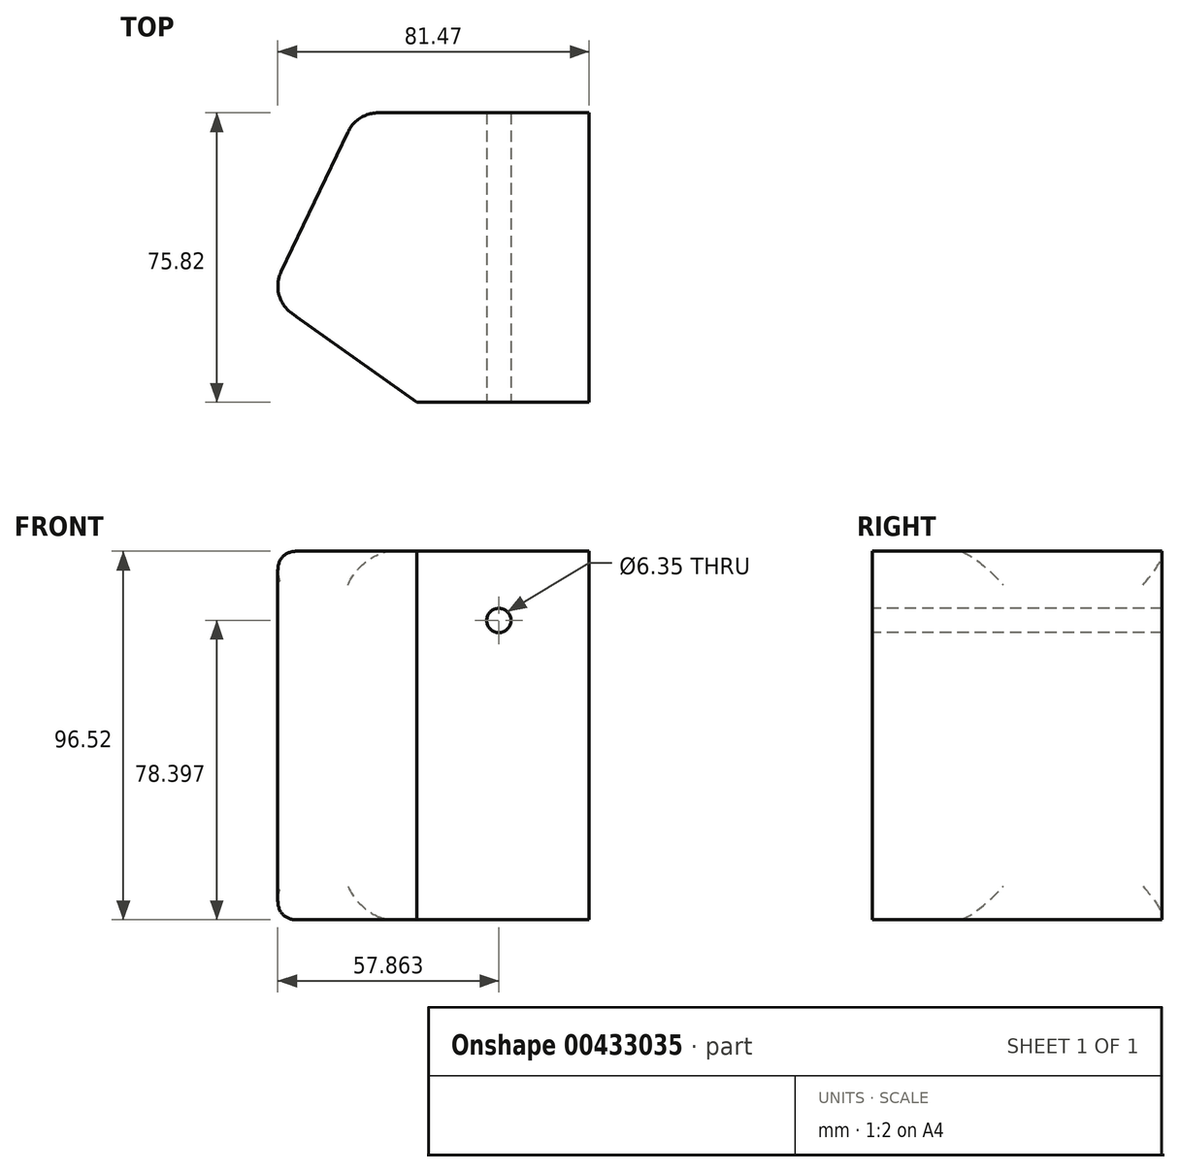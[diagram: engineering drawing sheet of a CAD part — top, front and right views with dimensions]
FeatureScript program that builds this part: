
annotation { "Feature Type Name" : "Feature", "Feature Type Description" : "" }
export const myFeature = defineFeature(function(context is Context, id is Id, definition is map)
    precondition{}
    {
        {
            var Q0;
            Q0=qCreatedBy(makeId("Top.planeOp"),FACE);
            var sketch = newSketch(context, id + "F0", { "sketchPlane" : qUnion([Q0])});
            skLineSegment(sketch, "E0", {"start": v(15.67, -27.58) * mm, "end": v(60.7, -27.58) * mm});
            skLineSegment(sketch, "E1", {"start": v(60.7, -27.58) * mm, "end": v(60.7, 48.24) * mm});
            skLineSegment(sketch, "E2", {"start": v(60.7, 48.24) * mm, "end": v(0, 48.24) * mm});
            skLineSegment(sketch, "E3", {"start": v(0, 48.24) * mm, "end": v(-23.09, 0) * mm});
            skLineSegment(sketch, "E4", {"start": v(-23.09, 0) * mm, "end": v(15.67, -27.58) * mm});
            skSolve(sketch);
        }
        {
            var Q0;
            Q0=makeQuery(id+"F0.imprint","IMPRINT",FACE,{"disambiguationData":[TD([[makeQuery(id+"F0.imprint","IMPRINT",EDGE,{"derivedFrom":sQuery(id+"F0.wireOp",EDGE,"E0")}),1.0]])]});
            extrude(context, id + "F1", {"entities" : qUnion([Q0]), "depth" : 96.52 * mm});
        }
        {
            var Q0;
            Q0=makeQuery(id+"F1.opExtrude","SWEPT_FACE",FACE,{"disambiguationData":[OSD([sQuery(id+"F0.wireOp",EDGE,"E3")])]});
            fillet(context, id + "F2", {"entities" : qUnion([Q0]), "radius" : 8.78 * mm, "tangentPropagation" : true, "allowEdgeOverflow" : false});
        }
        {
            var Q0;
            Q0=makeQuery(id+"F1.opExtrude","SWEPT_FACE",FACE,{"disambiguationData":[OSD([sQuery(id+"F0.wireOp",EDGE,"E0")])]});
            var sketch = newSketch(context, id + "F3", { "sketchPlane" : qUnion([Q0])});
            skCircle(sketch, "E5", {"center": v(37.1, 78.4) * mm, "radius": 11.72 * mm});
            skSolve(sketch);
        }
        {
            var Q0;
            Q0=sQuery(id+"F3.wireOp",VERTEX,"E5.center");
            var Q1;
            Q1=makeQuery(id+"F1.opExtrude","SWEPT_BODY",BODY,{"disambiguationData":[OSD([sQuery(id+"F0.wireOp",EDGE,"E0"),sQuery(id+"F0.wireOp",EDGE,"E1"),sQuery(id+"F0.wireOp",EDGE,"E2"),sQuery(id+"F0.wireOp",EDGE,"E3"),sQuery(id+"F0.wireOp",EDGE,"E4")])]});
            hole(context, id + "F4", {"style" : HoleStyle.SIMPLE, "endStyle" : HoleEndStyle.THROUGH, "holeDiameter" : 6.35 * mm, "isTappedThrough" : true, "tappedDepth" : 12.7 * mm, "tapClearance" : 3, "locations" : qUnion([Q0]), "scope" : qUnion([Q1])});
        }
    });
